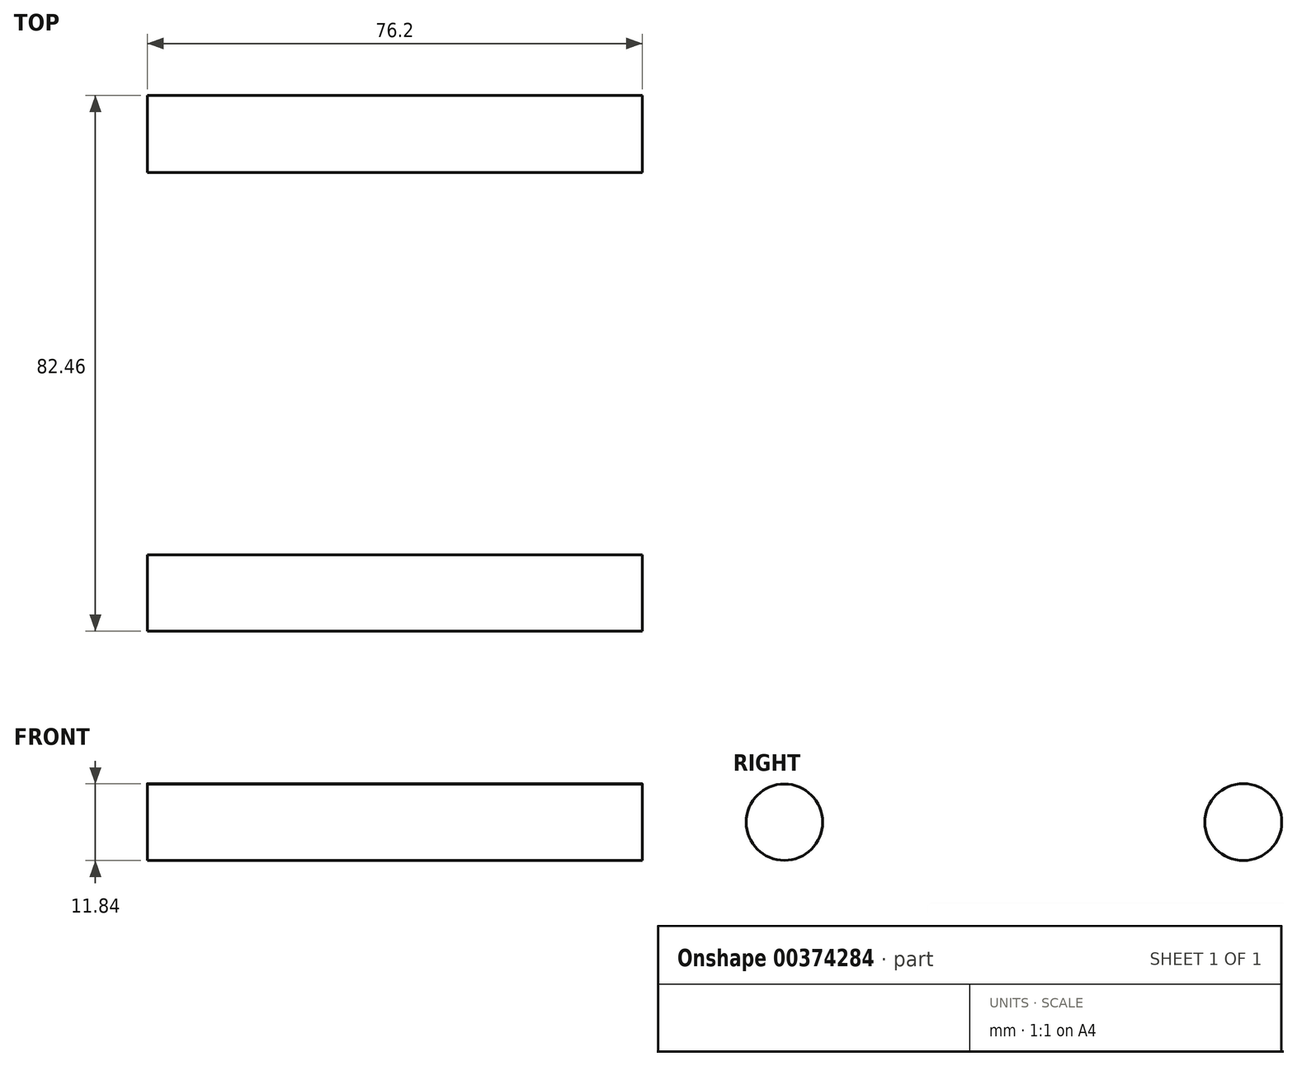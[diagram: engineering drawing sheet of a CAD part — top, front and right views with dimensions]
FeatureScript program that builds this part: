
annotation { "Feature Type Name" : "Feature", "Feature Type Description" : "" }
export const myFeature = defineFeature(function(context is Context, id is Id, definition is map)
    precondition{}
    {
        {
            var Q0;
            Q0=qCreatedBy(makeId("Right.planeOp"),FACE);
            var sketch = newSketch(context, id + "F0", { "sketchPlane" : qUnion([Q0])});
            skCircle(sketch, "E0", {"center": v(-38, 0) * mm, "radius": 5.88 * mm});
            skCircle(sketch, "E1", {"center": v(32.65, 0) * mm, "radius": 5.92 * mm});
            skSolve(sketch);
        }
        {
            var Q0;
            Q0=makeQuery(id+"F0.imprint","IMPRINT",FACE,{"disambiguationData":[TD([[makeQuery(id+"F0.imprint","IMPRINT",EDGE,{"derivedFrom":sQuery(id+"F0.wireOp",EDGE,"E0")}),1.0]])]});
            var Q1;
            Q1=makeQuery(id+"F0.imprint","IMPRINT",FACE,{"disambiguationData":[TD([[makeQuery(id+"F0.imprint","IMPRINT",EDGE,{"derivedFrom":sQuery(id+"F0.wireOp",EDGE,"E1")}),1.0]])]});
            extrude(context, id + "F1", {"entities" : qUnion([Q0, Q1]), "depth" : 76.2 * mm});
        }
    });
